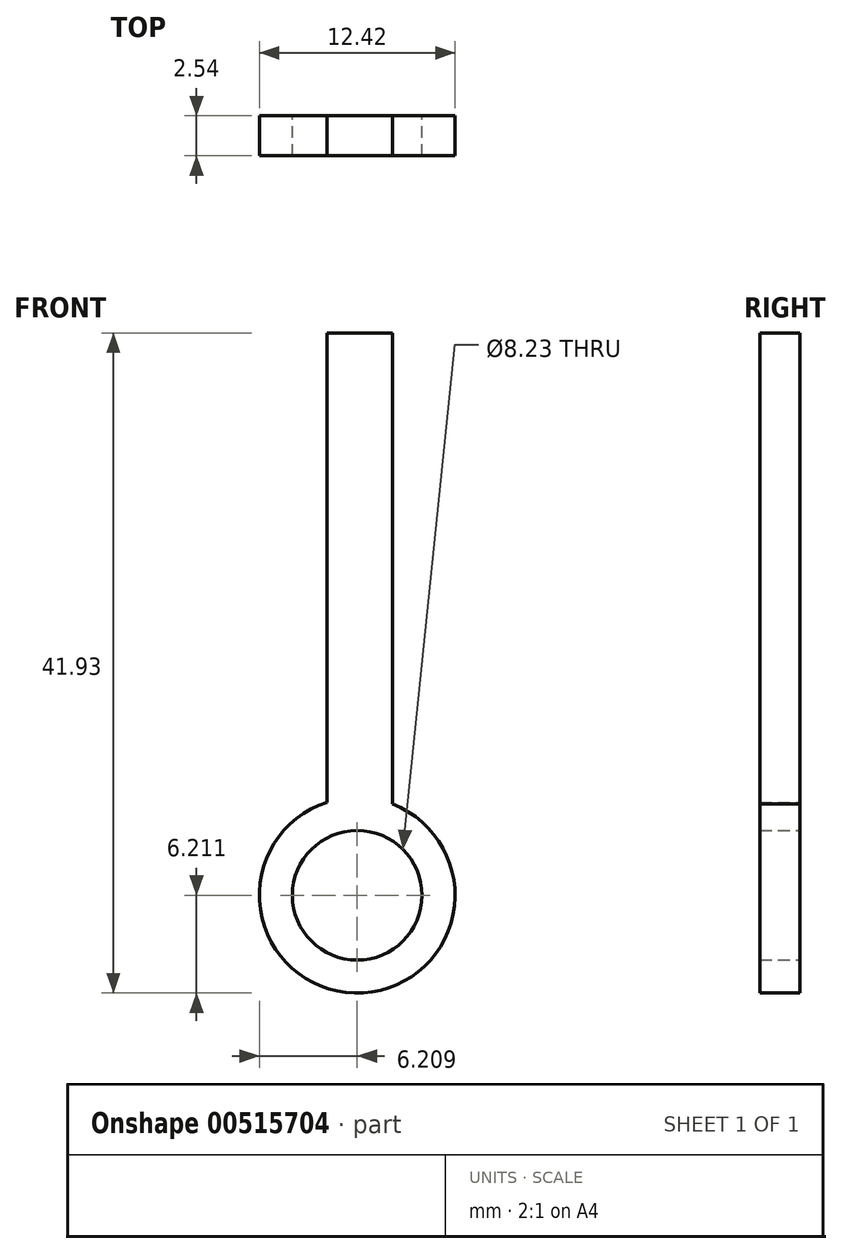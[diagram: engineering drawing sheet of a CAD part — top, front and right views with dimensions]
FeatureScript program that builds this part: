
annotation { "Feature Type Name" : "Feature", "Feature Type Description" : "" }
export const myFeature = defineFeature(function(context is Context, id is Id, definition is map)
    precondition{}
    {
        {
            var Q0;
            Q0=qCreatedBy(makeId("Front.planeOp"),FACE);
            var sketch = newSketch(context, id + "F0", { "sketchPlane" : qUnion([Q0])});
            skCircle(sketch, "E0", {"center": v(-17.02, -5.55) * mm, "radius": 4.12 * mm});
            skCircle(sketch, "E1", {"center": v(-17.02, -5.55) * mm, "radius": 6.21 * mm});
            skLineSegment(sketch, "E2", {"start": v(-14.78, 0.24) * mm, "end": v(-14.78, 30.17) * mm});
            skLineSegment(sketch, "E3", {"start": v(-18.94, 0.36) * mm, "end": v(-18.94, 30.17) * mm});
            skLineSegment(sketch, "E4", {"start": v(-18.94, 30.17) * mm, "end": v(-14.78, 30.17) * mm});
            skSolve(sketch);
        }
        {
            var Q0;
            {var subQ0=sQuery(id+"F0.wireOp",EDGE,"E2");Q0=makeQuery(id+"F0.imprint","IMPRINT",FACE,{"disambiguationData":[TD([[makeQuery(id+"F0.imprint","IMPRINT",EDGE,{"derivedFrom":subQ0}),1.0]])]});}
            var Q1;
            Q1=makeQuery(id+"F0.imprint","IMPRINT",FACE,{"disambiguationData":[TD([[makeQuery(id+"F0.imprint","IMPRINT",EDGE,{"derivedFrom":sQuery(id+"F0.wireOp",EDGE,"E0")}),-1.0]])]});
            extrude(context, id + "F1", {"entities" : qUnion([Q0, Q1]), "endBound" : BoundingType.SYMMETRIC, "depth" : 2.54 * mm, "offsetDistance" : 25.4 * mm});
        }
    });
